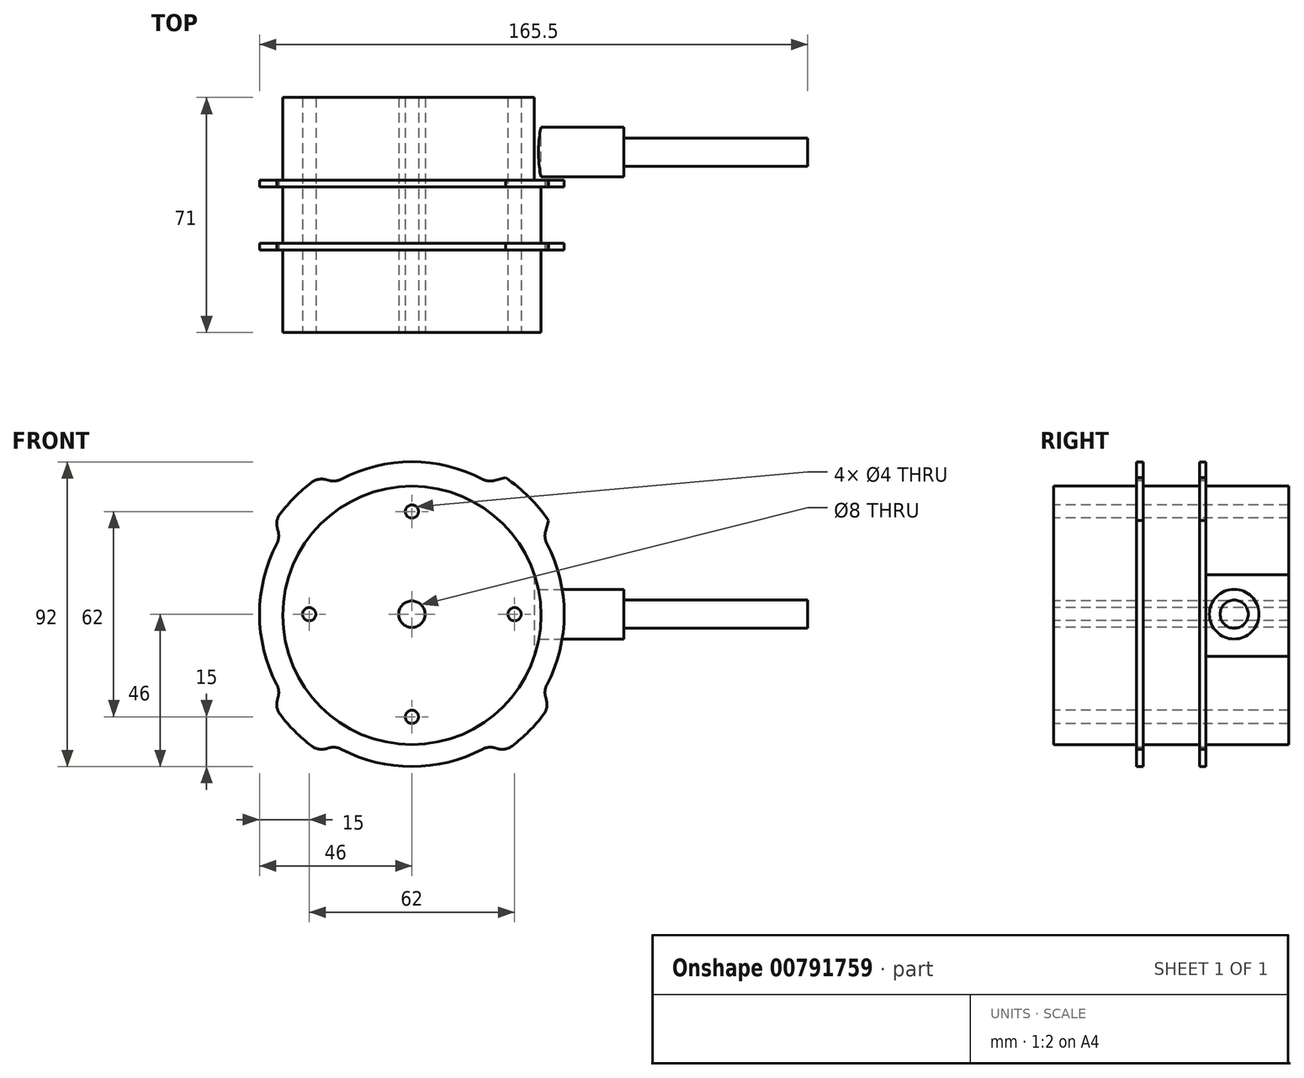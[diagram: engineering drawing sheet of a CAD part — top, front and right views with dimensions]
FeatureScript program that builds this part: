
annotation { "Feature Type Name" : "Feature", "Feature Type Description" : "" }
export const myFeature = defineFeature(function(context is Context, id is Id, definition is map)
    precondition{}
    {
        {
            var Q0;
            Q0=qCreatedBy(makeId("Front.planeOp"),FACE);
            var sketch = newSketch(context, id + "F0", { "sketchPlane" : qUnion([Q0])});
            skCircle(sketch, "E0", {"center": v(0, 0) * mm, "radius": 50 * mm});
            skSolve(sketch);
        }
        {
            var Q0;
            Q0 = qSketchRegion(id + "F0", true);
            extrude(context, id + "F1", {"entities" : qUnion([Q0]), "endBound" : BoundingType.SYMMETRIC, "depth" : 21 * mm, "offsetDistance" : 25 * mm});
        }
        {
            var Q0;
            Q0=qCreatedBy(makeId("Front.planeOp"),FACE);
            var sketch = newSketch(context, id + "F2", { "sketchPlane" : qUnion([Q0])});
            skCircle(sketch, "E1.0", {"center": v(0, 0) * mm, "radius": 50 * mm});
            skSolve(sketch);
        }
        {
            var Q0;
            Q0 = qSketchRegion(id + "F2", true);
            extrude(context, id + "F3", {"entities" : qUnion([Q0]), "operationType" : NewBodyOperationType.REMOVE, "endBound" : BoundingType.SYMMETRIC, "oppositeDirection" : true, "depth" : 17 * mm, "offsetDistance" : 25 * mm});
        }
        {
            var Q0;
            Q0=qCreatedBy(makeId("Front.planeOp"),FACE);
            var sketch = newSketch(context, id + "F4", { "sketchPlane" : qUnion([Q0])});
            skCircle(sketch, "E2", {"center": v(0, -0.36) * mm, "radius": 39 * mm});
            skSolve(sketch);
        }
        {
            var Q0;
            Q0 = qSketchRegion(id + "F4", true);
            extrude(context, id + "F5", {"entities" : qUnion([Q0]), "endBound" : BoundingType.SYMMETRIC, "depth" : 71 * mm, "offsetDistance" : 25 * mm});
        }
        {
            var Q0;
            Q0=qCreatedBy(makeId("Front.planeOp"),FACE);
            var sketch = newSketch(context, id + "F6", { "sketchPlane" : qUnion([Q0])});
            skCircle(sketch, "E3", {"center": v(0, 0) * mm, "radius": 46 * mm});
            skCircle(sketch, "E4.0", {"center": v(0, 0) * mm, "radius": 50 * mm});
            skLineSegment(sketch, "E5", {"start": v(0, 0) * mm, "end": v(-50, 0) * mm, "construction": true});
            skLineSegment(sketch, "E6", {"start": v(-50, 0) * mm, "end": v(50, 0) * mm, "construction": true});
            skLineSegment(sketch, "E7", {"start": v(0, -50) * mm, "end": v(0, 50) * mm, "construction": true});
            skLineSegment(sketch, "E8", {"start": v(-25, 43.3) * mm, "end": v(25, -43.3) * mm, "construction": true});
            skLineSegment(sketch, "E9", {"start": v(-43.3, 25) * mm, "end": v(43.3, -25) * mm, "construction": true});
            skLineSegment(sketch, "E10", {"start": v(-23, 39.84) * mm, "end": v(-28.26, 41.25) * mm});
            skLineSegment(sketch, "E11", {"start": v(-39.84, 23) * mm, "end": v(-41.25, 28.26) * mm});
            skLineSegment(sketch, "E12.MirrorCS", {"start": v(23, 39.84) * mm, "end": v(28.26, 41.25) * mm});
            skLineSegment(sketch, "E13.MirrorCS", {"start": v(39.84, 23) * mm, "end": v(41.25, 28.26) * mm});
            skLineSegment(sketch, "E14.MirrorCS", {"start": v(-43.3, -25) * mm, "end": v(43.3, 25) * mm, "construction": true});
            skLineSegment(sketch, "E15.MirrorCS", {"start": v(-23, -39.84) * mm, "end": v(-28.26, -41.25) * mm});
            skLineSegment(sketch, "E16.MirrorCS", {"start": v(23, -39.84) * mm, "end": v(28.26, -41.25) * mm});
            skLineSegment(sketch, "E17.MirrorCS", {"start": v(39.84, -23) * mm, "end": v(41.25, -28.26) * mm});
            skLineSegment(sketch, "E18.MirrorCS", {"start": v(-39.84, -23) * mm, "end": v(-41.25, -28.26) * mm});
            skSolve(sketch);
        }
        {
            var Q0;
            {var subQ0=sQuery(id+"F6.wireOp",EDGE,"E10");Q0=makeQuery(id+"F6.imprint","IMPRINT",FACE,{"disambiguationData":[TD([[makeQuery(id+"F6.imprint","IMPRINT",EDGE,{"derivedFrom":subQ0}),-1.0]])]});}
            var Q1;
            {var subQ0=sQuery(id+"F6.wireOp",EDGE,"E16.MirrorCS");Q1=makeQuery(id+"F6.imprint","IMPRINT",FACE,{"disambiguationData":[TD([[makeQuery(id+"F6.imprint","IMPRINT",EDGE,{"derivedFrom":subQ0}),-1.0]])]});}
            var Q2;
            {var subQ0=sQuery(id+"F6.wireOp",EDGE,"E11");Q2=makeQuery(id+"F6.imprint","IMPRINT",FACE,{"disambiguationData":[TD([[makeQuery(id+"F6.imprint","IMPRINT",EDGE,{"derivedFrom":subQ0}),1.0]])]});}
            var Q3;
            {var subQ0=sQuery(id+"F6.wireOp",EDGE,"E13.MirrorCS");Q3=makeQuery(id+"F6.imprint","IMPRINT",FACE,{"disambiguationData":[TD([[makeQuery(id+"F6.imprint","IMPRINT",EDGE,{"derivedFrom":subQ0}),-1.0]])]});}
            extrude(context, id + "F7", {"entities" : qUnion([Q0, Q1, Q2, Q3]), "operationType" : NewBodyOperationType.REMOVE, "endBound" : BoundingType.SYMMETRIC, "oppositeDirection" : true, "depth" : 25 * mm, "offsetDistance" : 25 * mm});
        }
        {
            var Q0;
            {var subQ0=sQuery(id+"F6.wireOp",EDGE,"E3");var subQ1=sQuery(id+"F6.wireOp",EDGE,"E10");Q0=makeQuery(id+"F7.boolean.opBoolean","COPY",EDGE,{"disambiguationData":[TD([makeQuery(id+"F1.opExtrude","CAP_FACE",FACE,{"disambiguationData":[OSD([sQuery(id+"F0.wireOp",EDGE,"E0")])],"isStart":false})])],"derivedFrom":makeQuery(id+"F7.opExtrude","SWEPT_EDGE",EDGE,{"disambiguationData":[OSD([subQ0,subQ1])]})});}
            var Q1;
            {var subQ0=sQuery(id+"F6.wireOp",EDGE,"E3");var subQ1=sQuery(id+"F6.wireOp",EDGE,"E10");Q1=makeQuery(id+"F7.boolean.opBoolean","COPY",EDGE,{"disambiguationData":[TD([makeQuery(id+"F1.opExtrude","CAP_FACE",FACE,{"disambiguationData":[OSD([sQuery(id+"F0.wireOp",EDGE,"E0")])],"isStart":true})])],"derivedFrom":makeQuery(id+"F7.opExtrude","SWEPT_EDGE",EDGE,{"disambiguationData":[OSD([subQ0,subQ1])]})});}
            var Q2;
            {var subQ0=sQuery(id+"F0.wireOp",EDGE,"E0");var subQ1=sQuery(id+"F6.wireOp",EDGE,"E10");Q2=makeQuery(id+"F7.boolean.opBoolean","COPY",EDGE,{"disambiguationData":[TD([makeQuery(id+"F1.opExtrude","CAP_FACE",FACE,{"disambiguationData":[OSD([subQ0])],"isStart":true})])],"derivedFrom":makeQuery(id+"F7.opExtrude","SWEPT_EDGE",EDGE,{"disambiguationData":[OSD([sQuery(id+"F6.wireOp",EDGE,"E4.0"),subQ1])]})});}
            var Q3;
            {var subQ0=sQuery(id+"F0.wireOp",EDGE,"E0");var subQ1=sQuery(id+"F6.wireOp",EDGE,"E10");Q3=makeQuery(id+"F7.boolean.opBoolean","COPY",EDGE,{"disambiguationData":[TD([makeQuery(id+"F1.opExtrude","CAP_FACE",FACE,{"disambiguationData":[OSD([subQ0])],"isStart":false})])],"derivedFrom":makeQuery(id+"F7.opExtrude","SWEPT_EDGE",EDGE,{"disambiguationData":[OSD([sQuery(id+"F6.wireOp",EDGE,"E4.0"),subQ1])]})});}
            var Q4;
            {var subQ0=sQuery(id+"F0.wireOp",EDGE,"E0");var subQ1=sQuery(id+"F6.wireOp",EDGE,"E11");Q4=makeQuery(id+"F7.boolean.opBoolean","COPY",EDGE,{"disambiguationData":[TD([makeQuery(id+"F1.opExtrude","CAP_FACE",FACE,{"disambiguationData":[OSD([subQ0])],"isStart":false})])],"derivedFrom":makeQuery(id+"F7.opExtrude","SWEPT_EDGE",EDGE,{"disambiguationData":[OSD([sQuery(id+"F6.wireOp",EDGE,"E4.0"),subQ1])]})});}
            var Q5;
            {var subQ0=sQuery(id+"F6.wireOp",EDGE,"E3");var subQ1=sQuery(id+"F6.wireOp",EDGE,"E11");Q5=makeQuery(id+"F7.boolean.opBoolean","COPY",EDGE,{"disambiguationData":[TD([makeQuery(id+"F1.opExtrude","CAP_FACE",FACE,{"disambiguationData":[OSD([sQuery(id+"F0.wireOp",EDGE,"E0")])],"isStart":false})])],"derivedFrom":makeQuery(id+"F7.opExtrude","SWEPT_EDGE",EDGE,{"disambiguationData":[OSD([subQ0,subQ1])]})});}
            var Q6;
            {var subQ0=sQuery(id+"F6.wireOp",EDGE,"E3");var subQ1=sQuery(id+"F6.wireOp",EDGE,"E11");Q6=makeQuery(id+"F7.boolean.opBoolean","COPY",EDGE,{"disambiguationData":[TD([makeQuery(id+"F1.opExtrude","CAP_FACE",FACE,{"disambiguationData":[OSD([sQuery(id+"F0.wireOp",EDGE,"E0")])],"isStart":true})])],"derivedFrom":makeQuery(id+"F7.opExtrude","SWEPT_EDGE",EDGE,{"disambiguationData":[OSD([subQ0,subQ1])]})});}
            var Q7;
            {var subQ0=sQuery(id+"F0.wireOp",EDGE,"E0");var subQ1=sQuery(id+"F6.wireOp",EDGE,"E11");Q7=makeQuery(id+"F7.boolean.opBoolean","COPY",EDGE,{"disambiguationData":[TD([makeQuery(id+"F1.opExtrude","CAP_FACE",FACE,{"disambiguationData":[OSD([subQ0])],"isStart":true})])],"derivedFrom":makeQuery(id+"F7.opExtrude","SWEPT_EDGE",EDGE,{"disambiguationData":[OSD([sQuery(id+"F6.wireOp",EDGE,"E4.0"),subQ1])]})});}
            var Q8;
            {var subQ0=sQuery(id+"F6.wireOp",EDGE,"E3");var subQ1=sQuery(id+"F6.wireOp",EDGE,"E12.MirrorCS");Q8=makeQuery(id+"F7.boolean.opBoolean","COPY",EDGE,{"disambiguationData":[TD([makeQuery(id+"F1.opExtrude","CAP_FACE",FACE,{"disambiguationData":[OSD([sQuery(id+"F0.wireOp",EDGE,"E0")])],"isStart":true})])],"derivedFrom":makeQuery(id+"F7.opExtrude","SWEPT_EDGE",EDGE,{"disambiguationData":[OSD([subQ0,subQ1])]})});}
            var Q9;
            {var subQ0=sQuery(id+"F0.wireOp",EDGE,"E0");var subQ1=sQuery(id+"F6.wireOp",EDGE,"E12.MirrorCS");Q9=makeQuery(id+"F7.boolean.opBoolean","COPY",EDGE,{"disambiguationData":[TD([makeQuery(id+"F1.opExtrude","CAP_FACE",FACE,{"disambiguationData":[OSD([subQ0])],"isStart":true})])],"derivedFrom":makeQuery(id+"F7.opExtrude","SWEPT_EDGE",EDGE,{"disambiguationData":[OSD([sQuery(id+"F6.wireOp",EDGE,"E4.0"),subQ1])]})});}
            var Q10;
            {var subQ0=sQuery(id+"F6.wireOp",EDGE,"E3");var subQ1=sQuery(id+"F6.wireOp",EDGE,"E12.MirrorCS");Q10=makeQuery(id+"F7.boolean.opBoolean","COPY",EDGE,{"disambiguationData":[TD([makeQuery(id+"F1.opExtrude","CAP_FACE",FACE,{"disambiguationData":[OSD([sQuery(id+"F0.wireOp",EDGE,"E0")])],"isStart":false})])],"derivedFrom":makeQuery(id+"F7.opExtrude","SWEPT_EDGE",EDGE,{"disambiguationData":[OSD([subQ0,subQ1])]})});}
            var Q11;
            {var subQ0=sQuery(id+"F0.wireOp",EDGE,"E0");var subQ1=sQuery(id+"F6.wireOp",EDGE,"E12.MirrorCS");Q11=makeQuery(id+"F7.boolean.opBoolean","COPY",EDGE,{"disambiguationData":[TD([makeQuery(id+"F1.opExtrude","CAP_FACE",FACE,{"disambiguationData":[OSD([subQ0])],"isStart":false})])],"derivedFrom":makeQuery(id+"F7.opExtrude","SWEPT_EDGE",EDGE,{"disambiguationData":[OSD([sQuery(id+"F6.wireOp",EDGE,"E4.0"),subQ1])]})});}
            var Q12;
            {var subQ0=sQuery(id+"F6.wireOp",EDGE,"E13.MirrorCS");var subQ1=sQuery(id+"F6.wireOp",EDGE,"E3");Q12=makeQuery(id+"F7.boolean.opBoolean","COPY",EDGE,{"disambiguationData":[TD([makeQuery(id+"F1.opExtrude","CAP_FACE",FACE,{"disambiguationData":[OSD([sQuery(id+"F0.wireOp",EDGE,"E0")])],"isStart":true})])],"derivedFrom":makeQuery(id+"F7.opExtrude","SWEPT_EDGE",EDGE,{"disambiguationData":[OSD([subQ1,subQ0])]})});}
            var Q13;
            {var subQ0=sQuery(id+"F0.wireOp",EDGE,"E0");var subQ1=sQuery(id+"F6.wireOp",EDGE,"E13.MirrorCS");Q13=makeQuery(id+"F7.boolean.opBoolean","COPY",EDGE,{"disambiguationData":[TD([makeQuery(id+"F1.opExtrude","CAP_FACE",FACE,{"disambiguationData":[OSD([subQ0])],"isStart":true})])],"derivedFrom":makeQuery(id+"F7.opExtrude","SWEPT_EDGE",EDGE,{"disambiguationData":[OSD([sQuery(id+"F6.wireOp",EDGE,"E4.0"),subQ1])]})});}
            var Q14;
            {var subQ0=sQuery(id+"F0.wireOp",EDGE,"E0");var subQ1=sQuery(id+"F6.wireOp",EDGE,"E13.MirrorCS");Q14=makeQuery(id+"F7.boolean.opBoolean","COPY",EDGE,{"disambiguationData":[TD([makeQuery(id+"F1.opExtrude","CAP_FACE",FACE,{"disambiguationData":[OSD([subQ0])],"isStart":false})])],"derivedFrom":makeQuery(id+"F7.opExtrude","SWEPT_EDGE",EDGE,{"disambiguationData":[OSD([sQuery(id+"F6.wireOp",EDGE,"E4.0"),subQ1])]})});}
            var Q15;
            {var subQ0=sQuery(id+"F6.wireOp",EDGE,"E13.MirrorCS");var subQ1=sQuery(id+"F6.wireOp",EDGE,"E3");Q15=makeQuery(id+"F7.boolean.opBoolean","COPY",EDGE,{"disambiguationData":[TD([makeQuery(id+"F1.opExtrude","CAP_FACE",FACE,{"disambiguationData":[OSD([sQuery(id+"F0.wireOp",EDGE,"E0")])],"isStart":false})])],"derivedFrom":makeQuery(id+"F7.opExtrude","SWEPT_EDGE",EDGE,{"disambiguationData":[OSD([subQ1,subQ0])]})});}
            var Q16;
            {var subQ0=sQuery(id+"F6.wireOp",EDGE,"E17.MirrorCS");var subQ1=sQuery(id+"F6.wireOp",EDGE,"E3");Q16=makeQuery(id+"F7.boolean.opBoolean","COPY",EDGE,{"disambiguationData":[TD([makeQuery(id+"F1.opExtrude","CAP_FACE",FACE,{"disambiguationData":[OSD([sQuery(id+"F0.wireOp",EDGE,"E0")])],"isStart":true})])],"derivedFrom":makeQuery(id+"F7.opExtrude","SWEPT_EDGE",EDGE,{"disambiguationData":[OSD([subQ1,subQ0])]})});}
            var Q17;
            {var subQ0=sQuery(id+"F0.wireOp",EDGE,"E0");var subQ1=sQuery(id+"F6.wireOp",EDGE,"E17.MirrorCS");Q17=makeQuery(id+"F7.boolean.opBoolean","COPY",EDGE,{"disambiguationData":[TD([makeQuery(id+"F1.opExtrude","CAP_FACE",FACE,{"disambiguationData":[OSD([subQ0])],"isStart":true})])],"derivedFrom":makeQuery(id+"F7.opExtrude","SWEPT_EDGE",EDGE,{"disambiguationData":[OSD([sQuery(id+"F6.wireOp",EDGE,"E4.0"),subQ1])]})});}
            var Q18;
            {var subQ0=sQuery(id+"F6.wireOp",EDGE,"E3");var subQ1=sQuery(id+"F6.wireOp",EDGE,"E17.MirrorCS");Q18=makeQuery(id+"F7.boolean.opBoolean","COPY",EDGE,{"disambiguationData":[TD([makeQuery(id+"F1.opExtrude","CAP_FACE",FACE,{"disambiguationData":[OSD([sQuery(id+"F0.wireOp",EDGE,"E0")])],"isStart":false})])],"derivedFrom":makeQuery(id+"F7.opExtrude","SWEPT_EDGE",EDGE,{"disambiguationData":[OSD([subQ0,subQ1])]})});}
            var Q19;
            {var subQ0=sQuery(id+"F0.wireOp",EDGE,"E0");var subQ1=sQuery(id+"F6.wireOp",EDGE,"E17.MirrorCS");Q19=makeQuery(id+"F7.boolean.opBoolean","COPY",EDGE,{"disambiguationData":[TD([makeQuery(id+"F1.opExtrude","CAP_FACE",FACE,{"disambiguationData":[OSD([subQ0])],"isStart":false})])],"derivedFrom":makeQuery(id+"F7.opExtrude","SWEPT_EDGE",EDGE,{"disambiguationData":[OSD([sQuery(id+"F6.wireOp",EDGE,"E4.0"),subQ1])]})});}
            var Q20;
            {var subQ0=sQuery(id+"F0.wireOp",EDGE,"E0");var subQ1=sQuery(id+"F6.wireOp",EDGE,"E16.MirrorCS");Q20=makeQuery(id+"F7.boolean.opBoolean","COPY",EDGE,{"disambiguationData":[TD([makeQuery(id+"F1.opExtrude","CAP_FACE",FACE,{"disambiguationData":[OSD([subQ0])],"isStart":true})])],"derivedFrom":makeQuery(id+"F7.opExtrude","SWEPT_EDGE",EDGE,{"disambiguationData":[OSD([sQuery(id+"F6.wireOp",EDGE,"E4.0"),subQ1])]})});}
            var Q21;
            {var subQ0=sQuery(id+"F6.wireOp",EDGE,"E16.MirrorCS");var subQ1=sQuery(id+"F6.wireOp",EDGE,"E3");Q21=makeQuery(id+"F7.boolean.opBoolean","COPY",EDGE,{"disambiguationData":[TD([makeQuery(id+"F1.opExtrude","CAP_FACE",FACE,{"disambiguationData":[OSD([sQuery(id+"F0.wireOp",EDGE,"E0")])],"isStart":true})])],"derivedFrom":makeQuery(id+"F7.opExtrude","SWEPT_EDGE",EDGE,{"disambiguationData":[OSD([subQ1,subQ0])]})});}
            var Q22;
            {var subQ0=sQuery(id+"F0.wireOp",EDGE,"E0");var subQ1=sQuery(id+"F6.wireOp",EDGE,"E16.MirrorCS");Q22=makeQuery(id+"F7.boolean.opBoolean","COPY",EDGE,{"disambiguationData":[TD([makeQuery(id+"F1.opExtrude","CAP_FACE",FACE,{"disambiguationData":[OSD([subQ0])],"isStart":false})])],"derivedFrom":makeQuery(id+"F7.opExtrude","SWEPT_EDGE",EDGE,{"disambiguationData":[OSD([sQuery(id+"F6.wireOp",EDGE,"E4.0"),subQ1])]})});}
            var Q23;
            {var subQ0=sQuery(id+"F6.wireOp",EDGE,"E16.MirrorCS");var subQ1=sQuery(id+"F6.wireOp",EDGE,"E3");Q23=makeQuery(id+"F7.boolean.opBoolean","COPY",EDGE,{"disambiguationData":[TD([makeQuery(id+"F1.opExtrude","CAP_FACE",FACE,{"disambiguationData":[OSD([sQuery(id+"F0.wireOp",EDGE,"E0")])],"isStart":false})])],"derivedFrom":makeQuery(id+"F7.opExtrude","SWEPT_EDGE",EDGE,{"disambiguationData":[OSD([subQ1,subQ0])]})});}
            var Q24;
            {var subQ0=sQuery(id+"F6.wireOp",EDGE,"E15.MirrorCS");var subQ1=sQuery(id+"F6.wireOp",EDGE,"E3");Q24=makeQuery(id+"F7.boolean.opBoolean","COPY",EDGE,{"disambiguationData":[TD([makeQuery(id+"F1.opExtrude","CAP_FACE",FACE,{"disambiguationData":[OSD([sQuery(id+"F0.wireOp",EDGE,"E0")])],"isStart":false})])],"derivedFrom":makeQuery(id+"F7.opExtrude","SWEPT_EDGE",EDGE,{"disambiguationData":[OSD([subQ1,subQ0])]})});}
            var Q25;
            {var subQ0=sQuery(id+"F6.wireOp",EDGE,"E3");var subQ1=sQuery(id+"F6.wireOp",EDGE,"E15.MirrorCS");Q25=makeQuery(id+"F7.boolean.opBoolean","COPY",EDGE,{"disambiguationData":[TD([makeQuery(id+"F1.opExtrude","CAP_FACE",FACE,{"disambiguationData":[OSD([sQuery(id+"F0.wireOp",EDGE,"E0")])],"isStart":true})])],"derivedFrom":makeQuery(id+"F7.opExtrude","SWEPT_EDGE",EDGE,{"disambiguationData":[OSD([subQ0,subQ1])]})});}
            var Q26;
            {var subQ0=sQuery(id+"F0.wireOp",EDGE,"E0");var subQ1=sQuery(id+"F6.wireOp",EDGE,"E15.MirrorCS");Q26=makeQuery(id+"F7.boolean.opBoolean","COPY",EDGE,{"disambiguationData":[TD([makeQuery(id+"F1.opExtrude","CAP_FACE",FACE,{"disambiguationData":[OSD([subQ0])],"isStart":true})])],"derivedFrom":makeQuery(id+"F7.opExtrude","SWEPT_EDGE",EDGE,{"disambiguationData":[OSD([sQuery(id+"F6.wireOp",EDGE,"E4.0"),subQ1])]})});}
            var Q27;
            {var subQ0=sQuery(id+"F0.wireOp",EDGE,"E0");var subQ1=sQuery(id+"F6.wireOp",EDGE,"E15.MirrorCS");Q27=makeQuery(id+"F7.boolean.opBoolean","COPY",EDGE,{"disambiguationData":[TD([makeQuery(id+"F1.opExtrude","CAP_FACE",FACE,{"disambiguationData":[OSD([subQ0])],"isStart":false})])],"derivedFrom":makeQuery(id+"F7.opExtrude","SWEPT_EDGE",EDGE,{"disambiguationData":[OSD([sQuery(id+"F6.wireOp",EDGE,"E4.0"),subQ1])]})});}
            var Q28;
            {var subQ0=sQuery(id+"F6.wireOp",EDGE,"E3");var subQ1=sQuery(id+"F6.wireOp",EDGE,"E18.MirrorCS");Q28=makeQuery(id+"F7.boolean.opBoolean","COPY",EDGE,{"disambiguationData":[TD([makeQuery(id+"F1.opExtrude","CAP_FACE",FACE,{"disambiguationData":[OSD([sQuery(id+"F0.wireOp",EDGE,"E0")])],"isStart":true})])],"derivedFrom":makeQuery(id+"F7.opExtrude","SWEPT_EDGE",EDGE,{"disambiguationData":[OSD([subQ0,subQ1])]})});}
            var Q29;
            {var subQ0=sQuery(id+"F0.wireOp",EDGE,"E0");var subQ1=sQuery(id+"F6.wireOp",EDGE,"E18.MirrorCS");Q29=makeQuery(id+"F7.boolean.opBoolean","COPY",EDGE,{"disambiguationData":[TD([makeQuery(id+"F1.opExtrude","CAP_FACE",FACE,{"disambiguationData":[OSD([subQ0])],"isStart":true})])],"derivedFrom":makeQuery(id+"F7.opExtrude","SWEPT_EDGE",EDGE,{"disambiguationData":[OSD([sQuery(id+"F6.wireOp",EDGE,"E4.0"),subQ1])]})});}
            var Q30;
            {var subQ0=sQuery(id+"F0.wireOp",EDGE,"E0");var subQ1=sQuery(id+"F6.wireOp",EDGE,"E18.MirrorCS");Q30=makeQuery(id+"F7.boolean.opBoolean","COPY",EDGE,{"disambiguationData":[TD([makeQuery(id+"F1.opExtrude","CAP_FACE",FACE,{"disambiguationData":[OSD([subQ0])],"isStart":false})])],"derivedFrom":makeQuery(id+"F7.opExtrude","SWEPT_EDGE",EDGE,{"disambiguationData":[OSD([sQuery(id+"F6.wireOp",EDGE,"E4.0"),subQ1])]})});}
            var Q31;
            {var subQ0=sQuery(id+"F6.wireOp",EDGE,"E3");var subQ1=sQuery(id+"F6.wireOp",EDGE,"E18.MirrorCS");Q31=makeQuery(id+"F7.boolean.opBoolean","COPY",EDGE,{"disambiguationData":[TD([makeQuery(id+"F1.opExtrude","CAP_FACE",FACE,{"disambiguationData":[OSD([sQuery(id+"F0.wireOp",EDGE,"E0")])],"isStart":false})])],"derivedFrom":makeQuery(id+"F7.opExtrude","SWEPT_EDGE",EDGE,{"disambiguationData":[OSD([subQ0,subQ1])]})});}
            fillet(context, id + "F8", {"entities" : qUnion([Q0, Q1, Q2, Q3, Q4, Q5, Q6, Q7, Q8, Q9, Q10, Q11, Q12, Q13, Q14, Q15, Q16, Q17, Q18, Q19, Q20, Q21, Q22, Q23, Q24, Q25, Q26, Q27, Q28, Q29, Q30, Q31]), "radius" : 5 * mm, "tangentPropagation" : true, "allowEdgeOverflow" : false});
        }
        {
            var Q0;
            Q0=makeQuery(id+"F5.opExtrude","CAP_FACE",FACE,{"disambiguationData":[OSD([sQuery(id+"F4.wireOp",EDGE,"E2")])],"isStart":false});
            var sketch = newSketch(context, id + "F9", { "sketchPlane" : qUnion([Q0])});
            skCircle(sketch, "E19", {"center": v(0, 31) * mm, "radius": 2 * mm});
            skCircle(sketch, "E20", {"center": v(0, 0) * mm, "radius": 31 * mm, "construction": true});
            skCircle(sketch, "E21", {"center": v(-31, 0) * mm, "radius": 2 * mm});
            skCircle(sketch, "E22", {"center": v(31, 0) * mm, "radius": 2 * mm});
            skCircle(sketch, "E23", {"center": v(0, -31) * mm, "radius": 2 * mm});
            skSolve(sketch);
        }
        {
            var Q0;
            Q0 = qSketchRegion(id + "F9", true);
            extrude(context, id + "F10", {"entities" : qUnion([Q0]), "operationType" : NewBodyOperationType.REMOVE, "endBound" : BoundingType.THROUGH_ALL, "oppositeDirection" : true, "depth" : 25 * mm, "offsetDistance" : 25 * mm});
        }
        {
            var Q0;
            Q0=qCreatedBy(makeId("Front.planeOp"),FACE);
            var sketch = newSketch(context, id + "F11", { "sketchPlane" : qUnion([Q0])});
            skCircle(sketch, "E24", {"center": v(0, 0) * mm, "radius": 4 * mm});
            skSolve(sketch);
        }
        {
            var Q0;
            Q0 = qSketchRegion(id + "F11", true);
            extrude(context, id + "F12", {"entities" : qUnion([Q0]), "depth" : 25 * mm, "offsetDistance" : 25 * mm});
        }
        {
            var Q0;
            Q0 = qSketchRegion(id + "F11", true);
            var Q1;
            Q1=makeQuery(id+"F5.opExtrude","CAP_FACE",FACE,{"disambiguationData":[OSD([sQuery(id+"F4.wireOp",EDGE,"E2")])],"isStart":false});
            var Q2;
            Q2=makeQuery(id+"F5.opExtrude","CAP_FACE",FACE,{"disambiguationData":[OSD([sQuery(id+"F4.wireOp",EDGE,"E2")])],"isStart":true});
            extrude(context, id + "F13", {"entities" : qUnion([Q0]), "operationType" : NewBodyOperationType.REMOVE, "endBound" : BoundingType.UP_TO_NEXT, "oppositeDirection" : true, "depth" : 25 * mm, "endBoundEntityFace" : qUnion([Q1]), "offsetDistance" : 25 * mm, "hasSecondDirection" : true, "secondDirectionBound" : SecondDirectionBoundingType.UP_TO_NEXT, "secondDirectionOppositeDirection" : false, "secondDirectionDepth" : 25 * mm, "secondDirectionBoundEntityFace" : qUnion([Q2])});
        }
        {
            var Q0;
            Q0 = qSketchRegion(id + "F11", true);
            var Q1;
            Q1=makeQuery(id+"F5.opExtrude","CAP_FACE",FACE,{"disambiguationData":[OSD([sQuery(id+"F4.wireOp",EDGE,"E2")])],"isStart":true});
            var Q2;
            Q2=makeQuery(id+"F5.opExtrude","CAP_FACE",FACE,{"disambiguationData":[OSD([sQuery(id+"F4.wireOp",EDGE,"E2")])],"isStart":false});
            extrude(context, id + "F14", {"entities" : qUnion([Q0]), "operationType" : NewBodyOperationType.REMOVE, "endBound" : BoundingType.UP_TO_SURFACE, "oppositeDirection" : true, "depth" : 25 * mm, "endBoundEntityFace" : qUnion([Q1]), "offsetDistance" : 25 * mm, "hasSecondDirection" : true, "secondDirectionBound" : SecondDirectionBoundingType.UP_TO_SURFACE, "secondDirectionOppositeDirection" : false, "secondDirectionDepth" : 25 * mm, "secondDirectionBoundEntityFace" : qUnion([Q2])});
        }
        {
            var Q0;
            Q0=makeQuery(id+"F3.boolean.opBoolean","SPLIT",BODY,{"disambiguationData":[OD(0.0)],"derivedFrom":makeQuery(id+"F1.opExtrude","SWEPT_BODY",BODY,{"disambiguationData":[OSD([sQuery(id+"F0.wireOp",EDGE,"E0")])]})});
            var Q1;
            Q1=makeQuery(id+"F3.boolean.opBoolean","SPLIT",BODY,{"disambiguationData":[OD(1.0)],"derivedFrom":makeQuery(id+"F1.opExtrude","SWEPT_BODY",BODY,{"disambiguationData":[OSD([sQuery(id+"F0.wireOp",EDGE,"E0")])]})});
            var Q2;
            Q2=makeQuery(id+"F5.opExtrude","SWEPT_BODY",BODY,{"disambiguationData":[OSD([sQuery(id+"F4.wireOp",EDGE,"E2")])]});
            booleanBodies(context, id + "F15", {"operationType" : BooleanOperationType.UNION, "tools" : qUnion([Q0, Q1, Q2])});
        }
        {
            var Q0;
            Q0=qCreatedBy(makeId("Right.planeOp"),FACE);
            cPlane(context, id + "F16", {"entities" : qUnion([Q0]), "cplaneType" : CPlaneType.OFFSET, "offset" : 39 * mm, "width" : 150 * mm, "height" : 150 * mm});
        }
        {
            var Q0;
            Q0=qCreatedBy(id+"F16.planeOp",FACE);
            var sketch = newSketch(context, id + "F17", { "sketchPlane" : qUnion([Q0])});
            skCircle(sketch, "E25", {"center": v(19, 0) * mm, "radius": 7.5 * mm});
            skLineSegment(sketch, "E26.0", {"start": v(10.5, -21.33) * mm, "end": v(10.5, 21.33) * mm, "construction": true});
            skSolve(sketch);
        }
        {
            var Q0;
            Q0 = qSketchRegion(id + "F17", true);
            extrude(context, id + "F18", {"entities" : qUnion([Q0]), "oppositeDirection" : true, "depth" : 2 * mm, "offsetDistance" : 25 * mm, "hasSecondDirection" : true, "secondDirectionOppositeDirection" : false, "secondDirectionDepth" : 25 * mm});
        }
        {
            var Q0;
            Q0=makeQuery(id+"F18.opExtrude","CAP_FACE",FACE,{"disambiguationData":[OSD([sQuery(id+"F17.wireOp",EDGE,"E25")])],"isStart":true});
            var sketch = newSketch(context, id + "F19", { "sketchPlane" : qUnion([Q0])});
            skCircle(sketch, "E27", {"center": v(19, 0) * mm, "radius": 4.25 * mm});
            skSolve(sketch);
        }
        {
            var Q0;
            Q0 = qSketchRegion(id + "F19", true);
            extrude(context, id + "F20", {"entities" : qUnion([Q0]), "operationType" : NewBodyOperationType.ADD, "depth" : 55.5 * mm, "offsetDistance" : 25 * mm});
        }
        {
            var Q0;
            Q0=makeQuery(id+"F5.opExtrude","CAP_FACE",FACE,{"disambiguationData":[OSD([sQuery(id+"F4.wireOp",EDGE,"E2")])],"isStart":true});
            var sketch = newSketch(context, id + "F21", { "sketchPlane" : qUnion([Q0])});
            skCircle(sketch, "E28.0", {"center": v(0, -0.36) * mm, "radius": 39 * mm});
            skLineSegment(sketch, "E29", {"start": v(-37, 11.96) * mm, "end": v(-37, -12.7) * mm});
            skSolve(sketch);
        }
        {
            var Q0;
            {var subQ0=sQuery(id+"F21.wireOp",EDGE,"E29");Q0=makeQuery(id+"F21.imprint","IMPRINT",FACE,{"disambiguationData":[TD([[makeQuery(id+"F21.imprint","IMPRINT",EDGE,{"derivedFrom":subQ0}),-1.0]])]});}
            var Q1;
            Q1=makeQuery(id+"F1.opExtrude","CAP_FACE",FACE,{"disambiguationData":[OSD([sQuery(id+"F0.wireOp",EDGE,"E0")])],"isStart":true});
            extrude(context, id + "F22", {"entities" : qUnion([Q0]), "operationType" : NewBodyOperationType.REMOVE, "endBound" : BoundingType.UP_TO_SURFACE, "oppositeDirection" : true, "depth" : 25 * mm, "endBoundEntityFace" : qUnion([Q1]), "offsetDistance" : 25 * mm});
        }
    });
